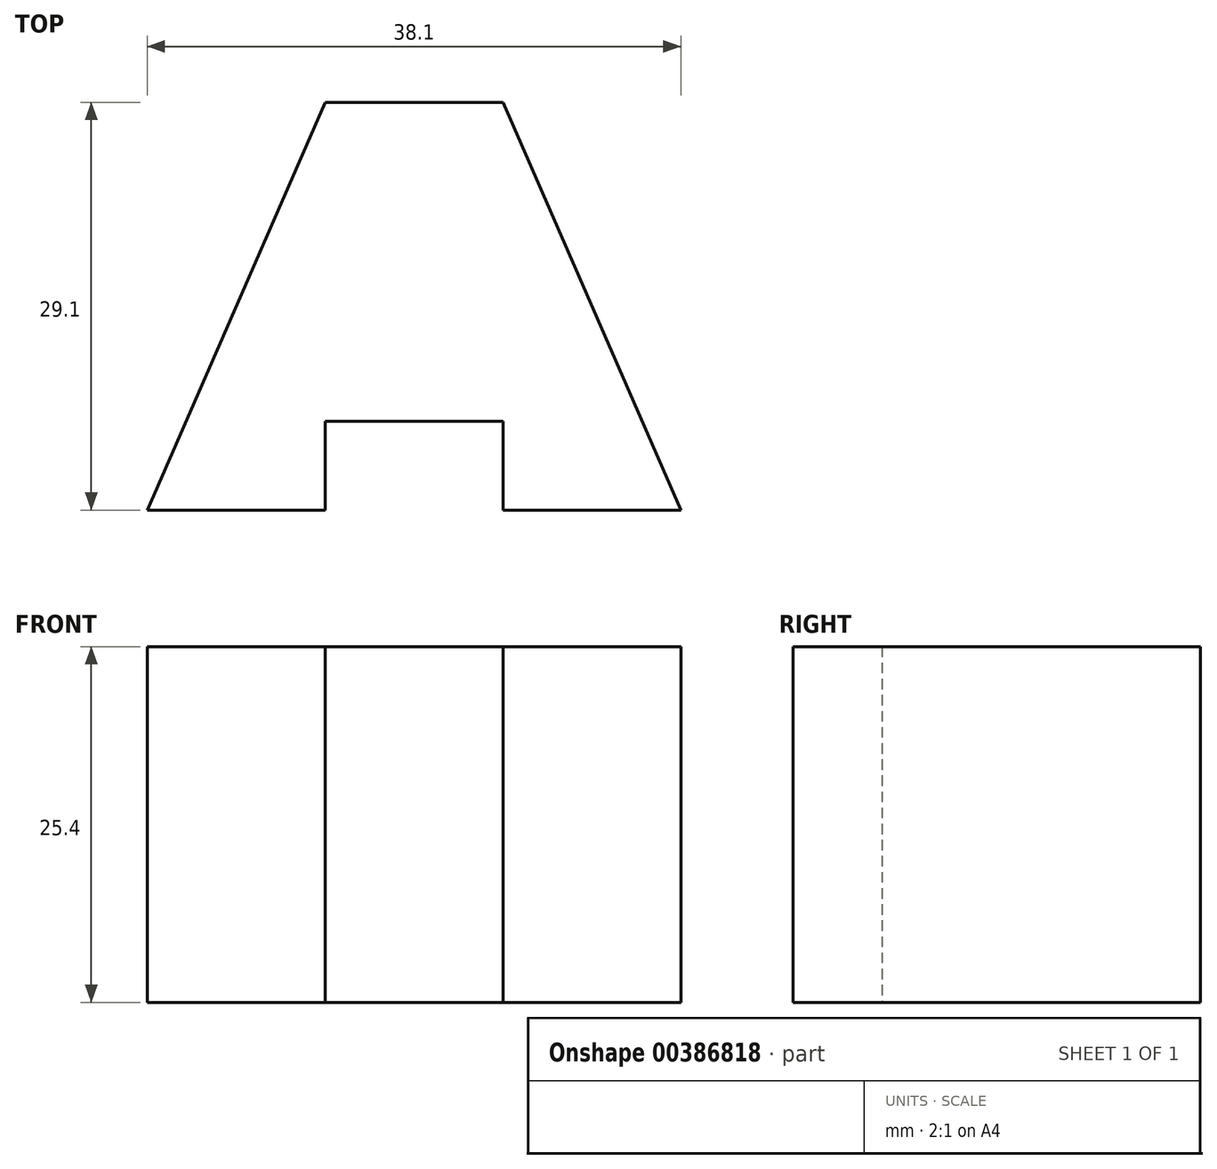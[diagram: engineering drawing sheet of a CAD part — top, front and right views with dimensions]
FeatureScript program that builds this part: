
annotation { "Feature Type Name" : "Feature", "Feature Type Description" : "" }
export const myFeature = defineFeature(function(context is Context, id is Id, definition is map)
    precondition{}
    {
        {
            var Q0;
            Q0=qCreatedBy(makeId("Top.planeOp"),FACE);
            var sketch = newSketch(context, id + "F0", { "sketchPlane" : qUnion([Q0])});
            skLineSegment(sketch, "E0", {"start": v(0, 0) * mm, "end": v(12.7, 0) * mm});
            skLineSegment(sketch, "E1", {"start": v(12.7, 0) * mm, "end": v(12.7, 6.35) * mm});
            skLineSegment(sketch, "E2", {"start": v(12.7, 6.35) * mm, "end": v(25.4, 6.35) * mm});
            skLineSegment(sketch, "E3", {"start": v(25.4, 6.35) * mm, "end": v(25.4, 0) * mm});
            skLineSegment(sketch, "E4", {"start": v(25.4, 0) * mm, "end": v(38.1, 0) * mm});
            skLineSegment(sketch, "E5", {"start": v(0, 0) * mm, "end": v(12.7, 29.1) * mm});
            skLineSegment(sketch, "E6", {"start": v(12.7, 29.1) * mm, "end": v(25.4, 29.1) * mm});
            skLineSegment(sketch, "E7", {"start": v(25.4, 29.1) * mm, "end": v(38.1, 0) * mm});
            skSolve(sketch);
        }
        {
            var Q0;
            Q0 = qSketchRegion(id + "F0", true);
            extrude(context, id + "F1", {"entities" : qUnion([Q0]), "depth" : 25.4 * mm});
        }
    });
